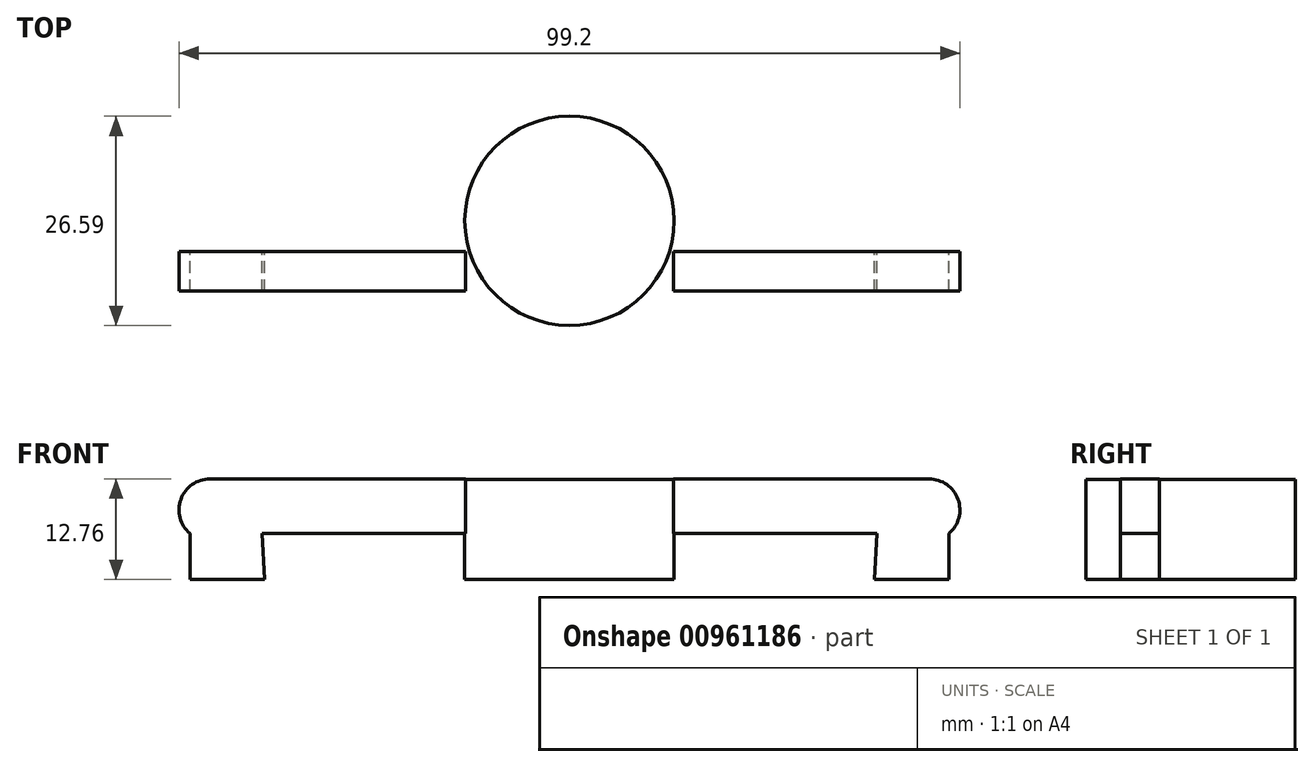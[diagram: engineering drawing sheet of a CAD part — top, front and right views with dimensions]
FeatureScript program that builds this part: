
annotation { "Feature Type Name" : "Feature", "Feature Type Description" : "" }
export const myFeature = defineFeature(function(context is Context, id is Id, definition is map)
    precondition{}
    {
        {
            var Q0;
            Q0=qCreatedBy(makeId("Top.planeOp"),FACE);
            var sketch = newSketch(context, id + "F0", { "sketchPlane" : qUnion([Q0])});
            skCircle(sketch, "E0", {"center": v(-7.4, 3.94) * mm, "radius": 13.3 * mm});
            skSolve(sketch);
        }
        {
            var Q0;
            Q0=makeQuery(id+"F0.imprint","IMPRINT",FACE,{"disambiguationData":[TD([[makeQuery(id+"F0.imprint","IMPRINT",EDGE,{"derivedFrom":sQuery(id+"F0.wireOp",EDGE,"E0")}),1.0]])]});
            extrude(context, id + "F1", {"entities" : qUnion([Q0]), "depth" : 12.7 * mm, "offsetDistance" : 25.4 * mm});
        }
        {
            var Q0;
            Q0=qCreatedBy(makeId("Front.planeOp"),FACE);
            var sketch = newSketch(context, id + "F2", { "sketchPlane" : qUnion([Q0])});
            skLineSegment(sketch, "E1", {"start": v(5.83, 12.76) * mm, "end": v(38.27, 12.76) * mm});
            skLineSegment(sketch, "E2", {"start": v(5.83, 12.76) * mm, "end": v(5.83, 5.83) * mm});
            skLineSegment(sketch, "E3", {"start": v(5.83, 5.83) * mm, "end": v(31.66, 5.83) * mm});
            skArc(sketch, "E4", {"start": v(40.8, 5.83) * mm, "mid": v(41.96, 10.18) * mm, "end": v(38.27, 12.76) * mm});
            skLineSegment(sketch, "E5", {"start": v(40.8, 5.83) * mm, "end": v(40.8, 0) * mm});
            skLineSegment(sketch, "E6", {"start": v(40.8, 0) * mm, "end": v(31.34, 0) * mm});
            skLineSegment(sketch, "E7", {"start": v(31.34, 0) * mm, "end": v(31.66, 5.83) * mm});
            skLineSegment(sketch, "E8.MirrorCS", {"start": v(-20.63, 12.76) * mm, "end": v(-53.08, 12.76) * mm});
            skLineSegment(sketch, "E9.MirrorCS", {"start": v(-20.63, 12.76) * mm, "end": v(-20.63, 5.83) * mm});
            skLineSegment(sketch, "E10.MirrorCS", {"start": v(-20.63, 5.83) * mm, "end": v(-46.46, 5.83) * mm});
            skLineSegment(sketch, "E11.MirrorCS", {"start": v(-46.15, 0) * mm, "end": v(-46.46, 5.83) * mm});
            skLineSegment(sketch, "E12.MirrorCS", {"start": v(-55.6, 0) * mm, "end": v(-46.15, 0) * mm});
            skLineSegment(sketch, "E13.MirrorCS", {"start": v(-55.6, 5.83) * mm, "end": v(-55.6, 0) * mm});
            skArc(sketch, "E14.MirrorCS", {"start": v(-55.6, 5.83) * mm, "mid": v(-56.76, 10.18) * mm, "end": v(-53.08, 12.76) * mm});
            skSolve(sketch);
        }
        {
            var Q0;
            Q0=makeQuery(id+"F2.imprint","IMPRINT",FACE,{"disambiguationData":[TD([[makeQuery(id+"F2.imprint","IMPRINT",EDGE,{"derivedFrom":sQuery(id+"F2.wireOp",EDGE,"E1")}),-1.0]])]});
            var Q1;
            Q1=makeQuery(id+"F2.imprint","IMPRINT",FACE,{"disambiguationData":[TD([[makeQuery(id+"F2.imprint","IMPRINT",EDGE,{"derivedFrom":sQuery(id+"F2.wireOp",EDGE,"E8.MirrorCS")}),1.0]])]});
            extrude(context, id + "F3", {"entities" : qUnion([Q0, Q1]), "depth" : 5 * mm, "offsetDistance" : 25.4 * mm});
        }
    });
